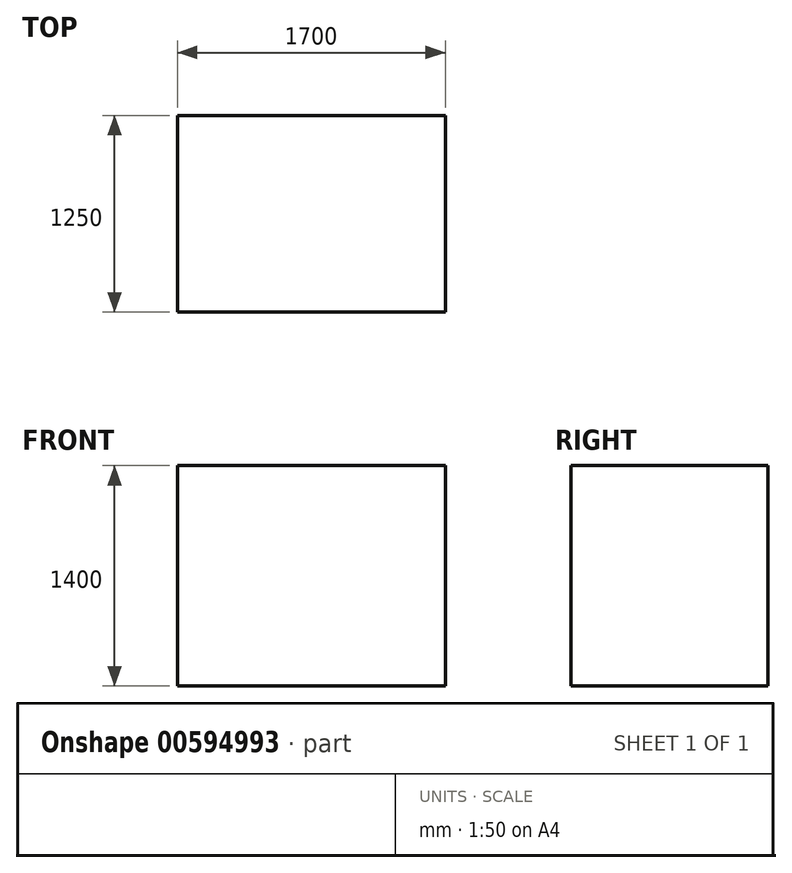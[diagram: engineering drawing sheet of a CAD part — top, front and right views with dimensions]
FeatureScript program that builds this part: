
annotation { "Feature Type Name" : "Feature", "Feature Type Description" : "" }
export const myFeature = defineFeature(function(context is Context, id is Id, definition is map)
    precondition{}
    {
        {
            var Q0;
            Q0=qCreatedBy(makeId("Front.planeOp"),FACE);
            var sketch = newSketch(context, id + "F0", { "sketchPlane" : qUnion([Q0])});
            skLineSegment(sketch, "E0.bottom", {"start": v(0, 0) * mm, "end": v(1700, 0) * mm});
            skLineSegment(sketch, "E0.top", {"start": v(0, 1400) * mm, "end": v(1700, 1400) * mm});
            skLineSegment(sketch, "E0.left", {"start": v(0, 0) * mm, "end": v(0, 1400) * mm});
            skLineSegment(sketch, "E0.right", {"start": v(1700, 0) * mm, "end": v(1700, 1400) * mm});
            skSolve(sketch);
        }
        {
            var Q0;
            Q0=makeQuery(id+"F0.imprint","IMPRINT",FACE,{"disambiguationData":[TD([[makeQuery(id+"F0.imprint","IMPRINT",EDGE,{"derivedFrom":sQuery(id+"F0.wireOp",EDGE,"E0.bottom")}),1.0]])]});
            extrude(context, id + "F1", {"entities" : qUnion([Q0]), "depth" : 1250 * mm, "offsetDistance" : 25 * mm});
        }
    });
